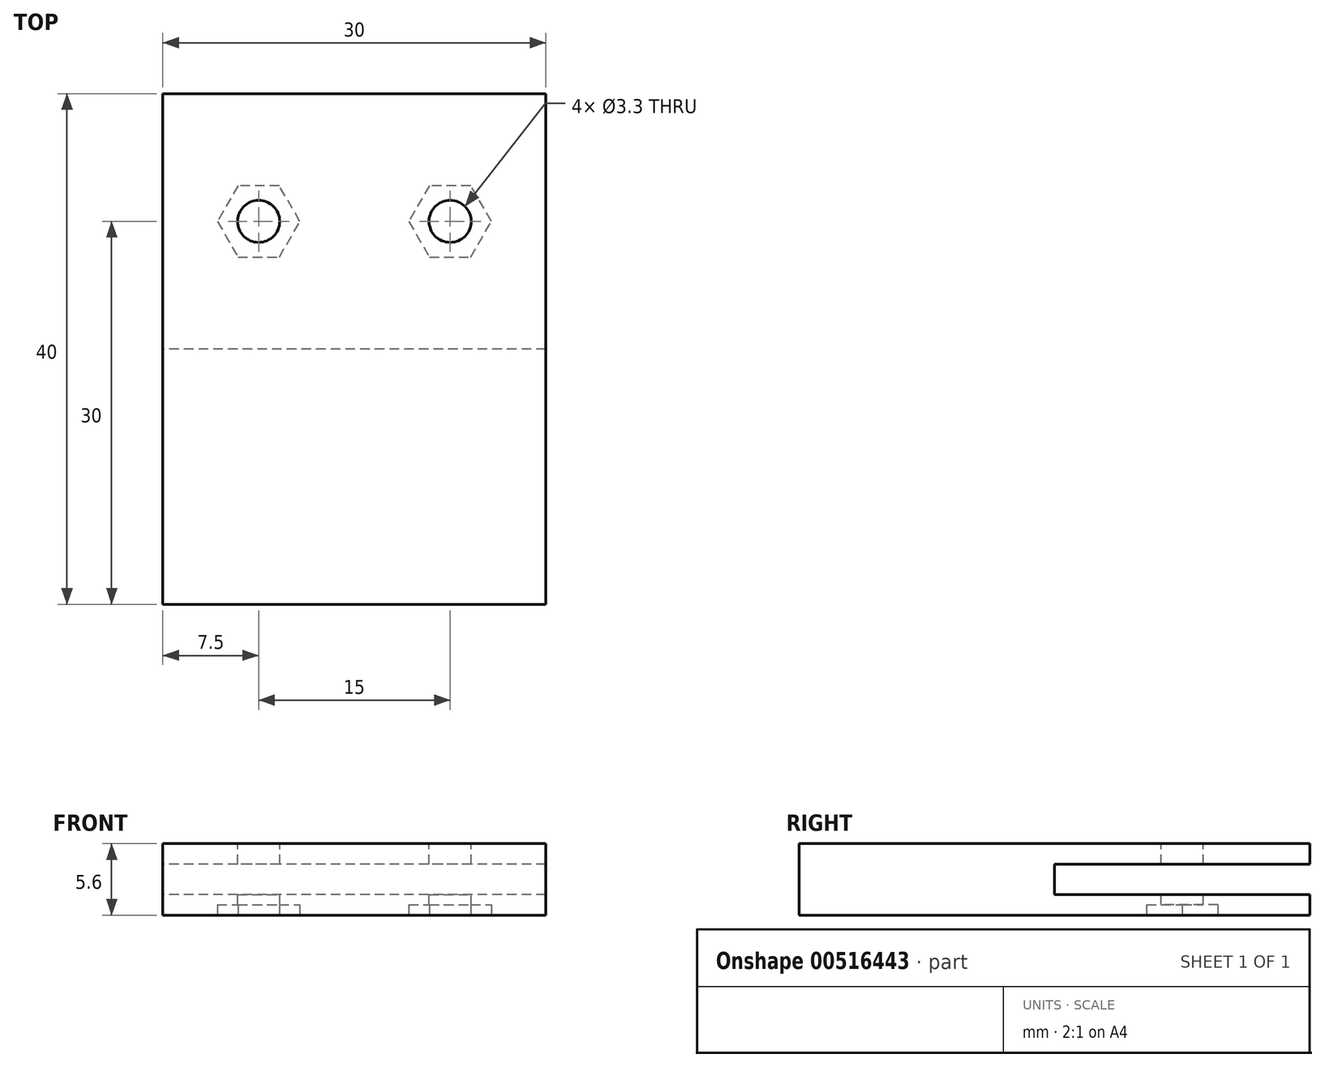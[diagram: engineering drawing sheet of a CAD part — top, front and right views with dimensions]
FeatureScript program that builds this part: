
annotation { "Feature Type Name" : "Feature", "Feature Type Description" : "" }
export const myFeature = defineFeature(function(context is Context, id is Id, definition is map)
    precondition{}
    {
        {
            var Q0;
            Q0=qCreatedBy(makeId("Right.planeOp"),FACE);
            var sketch = newSketch(context, id + "F0", { "sketchPlane" : qUnion([Q0])});
            skLineSegment(sketch, "E0", {"start": v(-20, 0) * mm, "end": v(20, 0) * mm});
            skLineSegment(sketch, "E1", {"start": v(20, 0) * mm, "end": v(20, 1.6) * mm});
            skLineSegment(sketch, "E2", {"start": v(20, 1.6) * mm, "end": v(0, 1.6) * mm});
            skLineSegment(sketch, "E3", {"start": v(0, 1.6) * mm, "end": v(0, 4) * mm});
            skLineSegment(sketch, "E4", {"start": v(0, 4) * mm, "end": v(20, 4) * mm});
            skLineSegment(sketch, "E5", {"start": v(20, 4) * mm, "end": v(20, 5.6) * mm});
            skLineSegment(sketch, "E6", {"start": v(20, 5.6) * mm, "end": v(-20, 5.6) * mm});
            skLineSegment(sketch, "E7", {"start": v(-20, 5.6) * mm, "end": v(-20, 0) * mm});
            skPoint(sketch, "E8.startSnap0", {"position": v(0, 5.6) * mm});
            skLineSegment(sketch, "E9", {"start": v(-20, 2.8) * mm, "end": v(20, 2.8) * mm, "construction": true});
            skPoint(sketch, "E9.startSnap0", {"position": v(0, 2.8) * mm});
            skLineSegment(sketch, "E10", {"start": v(20, 4.8) * mm, "end": v(-20, 4.8) * mm, "construction": true});
            skLineSegment(sketch, "E11", {"start": v(20, 0.8) * mm, "end": v(-20, 0.8) * mm, "construction": true});
            skSolve(sketch);
        }
        {
            var Q0;
            Q0=makeQuery(id+"F0.imprint","IMPRINT",FACE,{"disambiguationData":[TD([[makeQuery(id+"F0.imprint","IMPRINT",EDGE,{"derivedFrom":sQuery(id+"F0.wireOp",EDGE,"E0")}),1.0]])]});
            extrude(context, id + "F1", {"entities" : qUnion([Q0]), "depth" : 30 * mm, "offsetDistance" : 25 * mm});
        }
        {
            var Q0;
            {var subQ0=sQuery(id+"F0.wireOp",EDGE,"E6");Q0=makeQuery(id+"F1.opExtrude","SWEPT_FACE",FACE,{"disambiguationData":[OSD([subQ0]),TDD([makeQuery(id+"F0.imprint","IMPRINT",EDGE,{"disambiguationData":[TD([[makeQuery(id+"F0.imprint","INTERSECT",VERTEX,{"derivedFrom":[sQuery(id+"F0.wireOp",EDGE,"E5"),subQ0]}),-1.0]])],"derivedFrom":subQ0})])]});}
            var sketch = newSketch(context, id + "F2", { "sketchPlane" : qUnion([Q0])});
            skPoint(sketch, "E12.0", {"position": v(15, 20) * mm});
            skPoint(sketch, "E12.1", {"position": v(15, 20) * mm});
            skLineSegment(sketch, "E13", {"start": v(15, 20) * mm, "end": v(15, 20) * mm});
            skPoint(sketch, "E14.0", {"position": v(30, 0) * mm});
            skPoint(sketch, "E14.1", {"position": v(0, 0) * mm});
            skCircle(sketch, "E15", {"center": v(7.5, 10) * mm, "radius": 1.65 * mm});
            skCircle(sketch, "E16", {"center": v(22.5, 10) * mm, "radius": 1.65 * mm});
            skLineSegment(sketch, "E17", {"start": v(15, 20) * mm, "end": v(15, 0) * mm, "construction": true});
            skPoint(sketch, "E18", {"position": v(15, 10) * mm});
            skLineSegment(sketch, "E19", {"start": v(15, 10) * mm, "end": v(0, 10) * mm, "construction": true});
            skLineSegment(sketch, "E20", {"start": v(15, 10) * mm, "end": v(30, 10) * mm, "construction": true});
            skSolve(sketch);
        }
        {
            var Q0;
            Q0=makeQuery(id+"F2.imprint","IMPRINT",FACE,{"disambiguationData":[TD([[makeQuery(id+"F2.imprint","IMPRINT",EDGE,{"derivedFrom":sQuery(id+"F2.wireOp",EDGE,"E15")}),1.0]])]});
            var Q1;
            Q1=makeQuery(id+"F2.imprint","IMPRINT",FACE,{"disambiguationData":[TD([[makeQuery(id+"F2.imprint","IMPRINT",EDGE,{"derivedFrom":sQuery(id+"F2.wireOp",EDGE,"E16")}),1.0]])]});
            var Q2;
            {var subQ0=sQuery(id+"F0.wireOp",EDGE,"E0");Q2=makeQuery(id+"F1.opExtrude","SWEPT_FACE",FACE,{"disambiguationData":[OSD([subQ0]),TDD([makeQuery(id+"F0.imprint","IMPRINT",EDGE,{"disambiguationData":[TD([[makeQuery(id+"F0.imprint","INTERSECT",VERTEX,{"derivedFrom":[subQ0,sQuery(id+"F0.wireOp",EDGE,"E1")]}),1.0]])],"derivedFrom":subQ0})])]});}
            extrude(context, id + "F3", {"entities" : qUnion([Q0, Q1]), "operationType" : NewBodyOperationType.REMOVE, "endBound" : BoundingType.UP_TO_SURFACE, "oppositeDirection" : true, "depth" : 25 * mm, "endBoundEntityFace" : qUnion([Q2]), "offsetDistance" : 25 * mm});
        }
        {
            var Q0;
            {var subQ0=sQuery(id+"F0.wireOp",EDGE,"E0");Q0=makeQuery(id+"F1.opExtrude","SWEPT_FACE",FACE,{"disambiguationData":[OSD([subQ0]),TDD([makeQuery(id+"F0.imprint","IMPRINT",EDGE,{"disambiguationData":[TD([[makeQuery(id+"F0.imprint","INTERSECT",VERTEX,{"derivedFrom":[subQ0,sQuery(id+"F0.wireOp",EDGE,"E1")]}),1.0]])],"derivedFrom":subQ0})])]});}
            var sketch = newSketch(context, id + "F4", { "sketchPlane" : qUnion([Q0])});
            skPoint(sketch, "E21.0", {"position": v(7.5, -10) * mm});
            skPoint(sketch, "E21.1", {"position": v(22.5, -10) * mm});
            skCircle(sketch, "E22.cCircle", {"center": v(22.5, -10) * mm, "radius": 2.8 * mm, "construction": true});
            skLineSegment(sketch, "E22.0", {"start": v(24.12, -7.2) * mm, "end": v(25.73, -10) * mm});
            skLineSegment(sketch, "E22.1", {"start": v(25.73, -10) * mm, "end": v(24.12, -12.8) * mm});
            skLineSegment(sketch, "E22.2", {"start": v(24.12, -12.8) * mm, "end": v(20.88, -12.8) * mm});
            skLineSegment(sketch, "E22.3", {"start": v(20.88, -12.8) * mm, "end": v(19.27, -10) * mm});
            skLineSegment(sketch, "E22.4", {"start": v(19.27, -10) * mm, "end": v(20.88, -7.2) * mm});
            skLineSegment(sketch, "E22.5", {"start": v(20.88, -7.2) * mm, "end": v(24.12, -7.2) * mm});
            skPoint(sketch, "E22.0.midPoint", {"position": v(25.3, -10) * mm});
            skCircle(sketch, "E23.cCircle", {"center": v(7.5, -10) * mm, "radius": 2.8 * mm, "construction": true});
            skLineSegment(sketch, "E23.0", {"start": v(9.12, -7.2) * mm, "end": v(10.73, -10) * mm});
            skLineSegment(sketch, "E23.1", {"start": v(10.73, -10) * mm, "end": v(9.12, -12.8) * mm});
            skLineSegment(sketch, "E23.2", {"start": v(9.12, -12.8) * mm, "end": v(5.88, -12.8) * mm});
            skLineSegment(sketch, "E23.3", {"start": v(5.88, -12.8) * mm, "end": v(4.27, -10) * mm});
            skLineSegment(sketch, "E23.4", {"start": v(4.27, -10) * mm, "end": v(5.88, -7.2) * mm});
            skLineSegment(sketch, "E23.5", {"start": v(5.88, -7.2) * mm, "end": v(9.12, -7.2) * mm});
            skPoint(sketch, "E23.0.midPoint", {"position": v(10.3, -10) * mm});
            skSolve(sketch);
        }
        {
            var Q0;
            Q0 = qSketchRegion(id + "F4", true);
            extrude(context, id + "F5", {"entities" : qUnion([Q0]), "operationType" : NewBodyOperationType.REMOVE, "oppositeDirection" : true, "depth" : .8 * mm, "offsetDistance" : 25 * mm});
        }
    });
